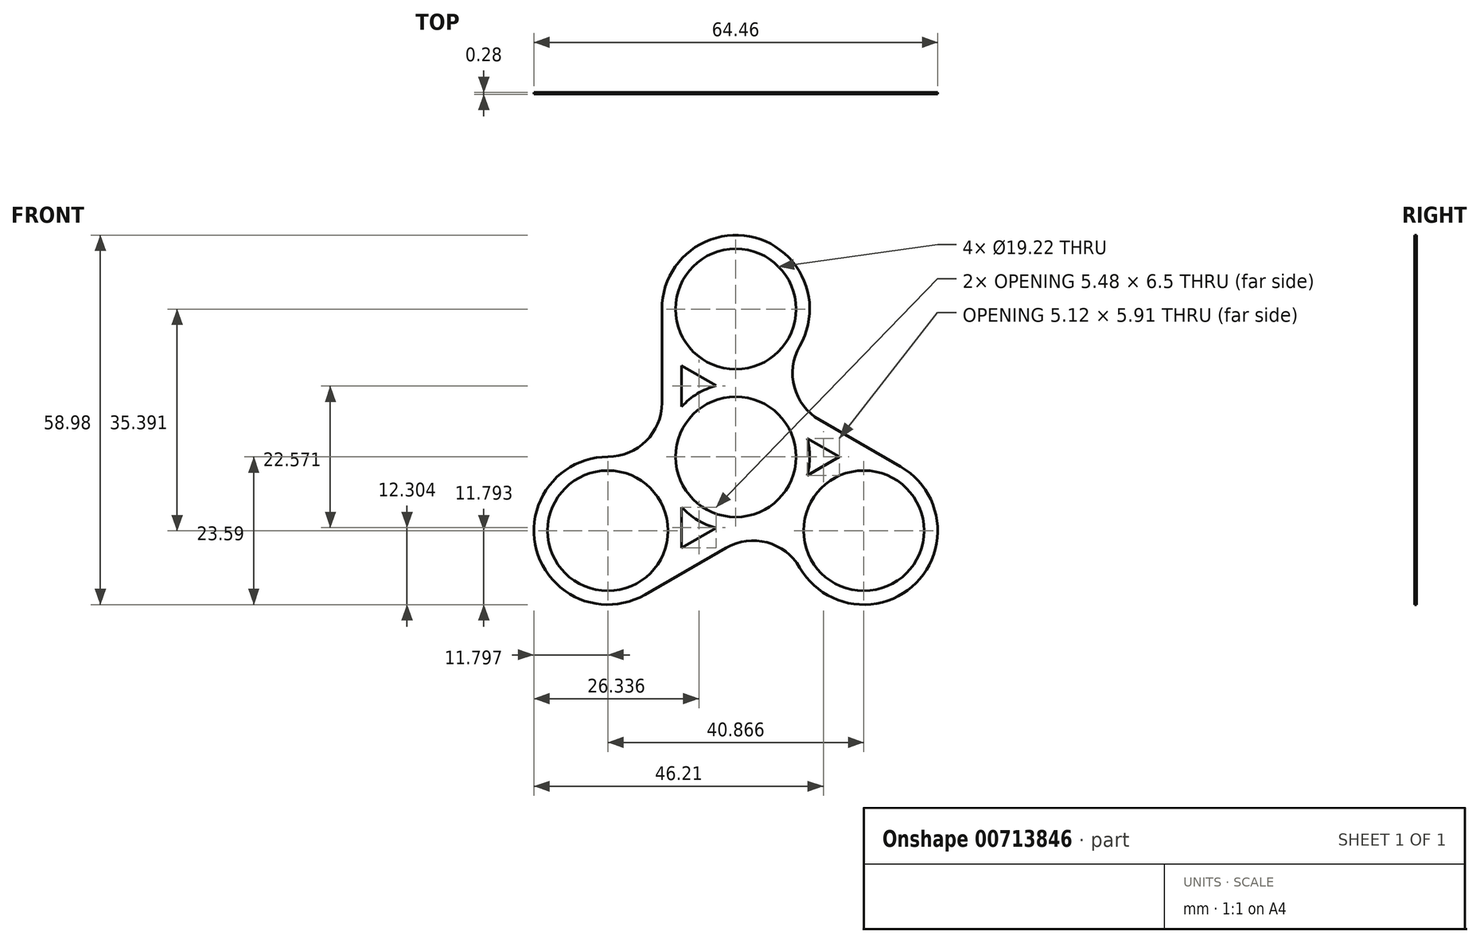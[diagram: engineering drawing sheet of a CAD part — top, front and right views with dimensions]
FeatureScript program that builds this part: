
annotation { "Feature Type Name" : "Feature", "Feature Type Description" : "" }
export const myFeature = defineFeature(function(context is Context, id is Id, definition is map)
    precondition{}
    {
        {
            assignVariable(context, id + "F0", {"name" : "th", "anyValue" : .276});
        }
        {
            var Q0;
            Q0=qCreatedBy(makeId("Front.planeOp"),FACE);
            var sketch = newSketch(context, id + "F1", { "sketchPlane" : qUnion([Q0])});
            skArc(sketch, "E0", {"start": v(-8.64, -8.04) * mm, "mid": v(-6.12, -10.08) * mm, "end": v(-3.15, -11.37) * mm});
            skArc(sketch, "E1", {"start": v(10.22, -17.7) * mm, "mid": v(28.77, -20.14) * mm, "end": v(26.33, -1.58) * mm});
            skArc(sketch, "E2", {"start": v(10.22, 17.7) * mm, "mid": v(3.05, 34.99) * mm, "end": v(-11.8, 23.6) * mm});
            skArc(sketch, "E3", {"start": v(-20.43, 0) * mm, "mid": v(-31.83, -14.85) * mm, "end": v(-14.53, -22.01) * mm});
            skLineSegment(sketch, "E4", {"start": v(-20.43, -11.8) * mm, "end": v(0, 23.6) * mm, "construction": true});
            skLineSegment(sketch, "E5", {"start": v(0, 23.6) * mm, "end": v(20.43, -11.8) * mm, "construction": true});
            skLineSegment(sketch, "E6", {"start": v(20.43, -11.8) * mm, "end": v(-20.43, -11.8) * mm, "construction": true});
            skLineSegment(sketch, "E7", {"start": v(0, 0) * mm, "end": v(0, 23.6) * mm, "construction": true});
            skLineSegment(sketch, "E8", {"start": v(0, 0) * mm, "end": v(20.43, -11.8) * mm, "construction": true});
            skLineSegment(sketch, "E9", {"start": v(0, 0) * mm, "end": v(-20.43, -11.8) * mm, "construction": true});
            skCircle(sketch, "E10", {"center": v(0, 0) * mm, "radius": 9.61 * mm});
            skCircle(sketch, "E11", {"center": v(0, 23.6) * mm, "radius": 9.61 * mm});
            skCircle(sketch, "E12", {"center": v(20.43, -11.8) * mm, "radius": 9.61 * mm});
            skCircle(sketch, "E13", {"center": v(-20.43, -11.8) * mm, "radius": 9.61 * mm});
            skCircle(sketch, "E14", {"center": v(0, 23.6) * mm, "radius": 4.38 * mm});
            skCircle(sketch, "E15", {"center": v(20.43, -11.8) * mm, "radius": 4.38 * mm});
            skCircle(sketch, "E16", {"center": v(-20.43, -11.8) * mm, "radius": 4.38 * mm});
            skCircle(sketch, "E17", {"center": v(-20.43, -11.8) * mm, "radius": 5.6 * mm});
            skCircle(sketch, "E18", {"center": v(20.43, -11.8) * mm, "radius": 5.6 * mm});
            skCircle(sketch, "E19", {"center": v(0, 23.6) * mm, "radius": 5.6 * mm});
            skLineSegment(sketch, "E20", {"start": v(-14.53, -22.01) * mm, "end": v(-1.58, -14.53) * mm});
            skLineSegment(sketch, "E21", {"start": v(26.33, -1.58) * mm, "end": v(13.38, 5.9) * mm});
            skLineSegment(sketch, "E22", {"start": v(-11.8, 0) * mm, "end": v(-11.8, 3.16) * mm, "construction": true});
            skPoint(sketch, "E23.startSnap0", {"position": v(10.22, 5.9) * mm});
            skPoint(sketch, "E23.endSnap0", {"position": v(10.22, 5.9) * mm});
            skPoint(sketch, "E24.endSnap0", {"position": v(-10.22, 5.9) * mm});
            skLineSegment(sketch, "E25", {"start": v(10.22, 17.7) * mm, "end": v(5.9, 10.22) * mm, "construction": true});
            skArc(sketch, "E26", {"start": v(10.22, 17.7) * mm, "mid": v(9.35, 11.14) * mm, "end": v(13.38, 5.9) * mm});
            skLineSegment(sketch, "E27", {"start": v(-20.43, 0) * mm, "end": v(-11.8, 0) * mm, "construction": true});
            skArc(sketch, "E28", {"start": v(-20.43, 0) * mm, "mid": v(-14.33, 2.53) * mm, "end": v(-11.8, 8.64) * mm});
            skArc(sketch, "E29", {"start": v(10.22, -17.7) * mm, "mid": v(4.97, -13.67) * mm, "end": v(-1.58, -14.53) * mm});
            skLineSegment(sketch, "E30", {"start": v(0, 0) * mm, "end": v(5.9, 10.22) * mm, "construction": true});
            skLineSegment(sketch, "E31", {"start": v(0, 0) * mm, "end": v(10.22, -17.7) * mm, "construction": true});
            skLineSegment(sketch, "E32.trimOffspring", {"start": v(-11.8, 8.64) * mm, "end": v(-11.8, 23.6) * mm});
            skLineSegment(sketch, "E33.trimOffspring", {"start": v(8.64, 8.64) * mm, "end": v(5.9, 10.22) * mm, "construction": true});
            skLineSegment(sketch, "E34", {"start": v(-8.64, -14.53) * mm, "end": v(-8.64, -8.04) * mm});
            skLineSegment(sketch, "E35", {"start": v(-8.64, 14.53) * mm, "end": v(-3.15, 11.37) * mm});
            skLineSegment(sketch, "E36", {"start": v(16.54, 0) * mm, "end": v(11.42, -2.95) * mm});
            skLineSegment(sketch, "E37.trimOffspring", {"start": v(-0.1, 9.61) * mm, "end": v(0, 9.55) * mm});
            skLineSegment(sketch, "E38.trimOffspring", {"start": v(-8.64, 8.04) * mm, "end": v(-8.64, 14.53) * mm});
            skLineSegment(sketch, "E39.trimOffspring", {"start": v(-8.64, -4.99) * mm, "end": v(-8.64, -4.22) * mm});
            skLineSegment(sketch, "E40.trimOffspring", {"start": v(-3.15, -11.37) * mm, "end": v(-8.64, -14.53) * mm});
            skArc(sketch, "E41.trimOffspring", {"start": v(-3.15, 11.37) * mm, "mid": v(-6.12, 10.08) * mm, "end": v(-8.64, 8.04) * mm});
            skArc(sketch, "E42.trimOffspring", {"start": v(11.42, -2.95) * mm, "mid": v(11.8, 0) * mm, "end": v(11.42, 2.95) * mm});
            skArc(sketch, "E43.trimOffspring", {"start": v(10.22, 5.9) * mm, "mid": v(8.34, 8.34) * mm, "end": v(5.9, 10.22) * mm, "construction": true});
            skLineSegment(sketch, "E44.trimOffspring", {"start": v(11.42, 2.95) * mm, "end": v(16.54, 0) * mm});
            skLineSegment(sketch, "E45.trimOffspring", {"start": v(8.38, -4.71) * mm, "end": v(8.27, -4.77) * mm});
            skCircle(sketch, "E46", {"center": v(0, 0) * mm, "radius": 5.6 * mm});
            skCircle(sketch, "E47", {"center": v(0, 0) * mm, "radius": 4.38 * mm});
            skSolve(sketch);
        }
        {
            var Q0;
            Q0 = qSketchRegion(id + "F1", true);
            extrude(context, id + "F2", {"entities" : qUnion([Q0]), "depth" : (getVariable(context, 'th')) * mm, "offsetDistance" : 25.4 * mm});
        }
    });
